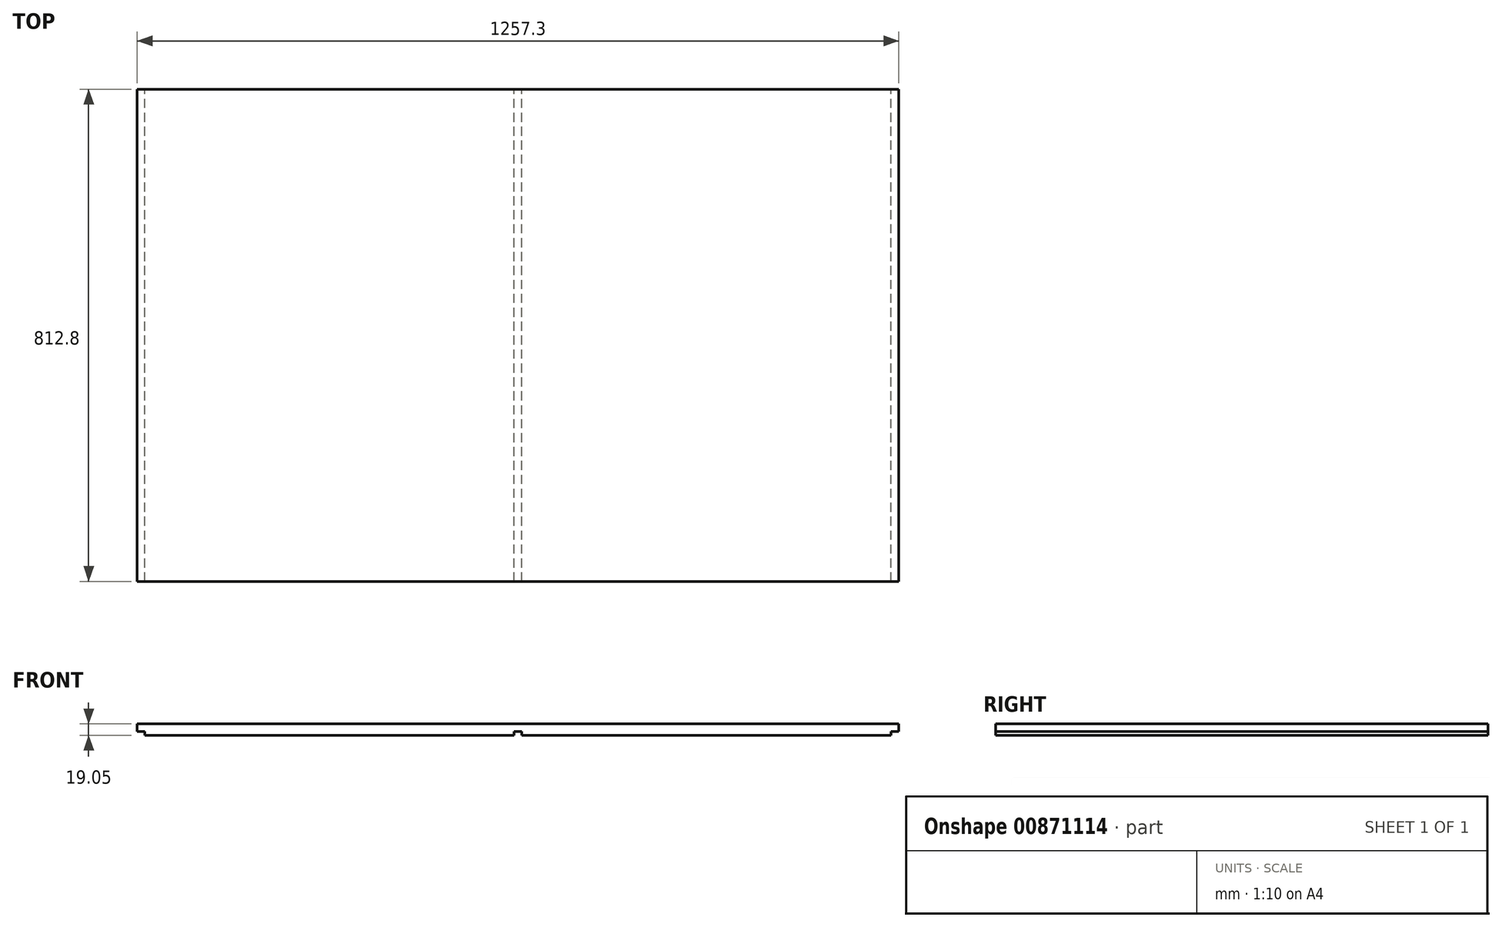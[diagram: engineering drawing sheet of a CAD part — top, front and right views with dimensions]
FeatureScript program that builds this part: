
annotation { "Feature Type Name" : "Feature", "Feature Type Description" : "" }
export const myFeature = defineFeature(function(context is Context, id is Id, definition is map)
    precondition{}
    {
        {
            var Q0;
            Q0=qCreatedBy(makeId("Front.planeOp"),FACE);
            var sketch = newSketch(context, id + "F0", { "sketchPlane" : qUnion([Q0])});
            skLineSegment(sketch, "E0.bottom", {"start": v(12.7, 0) * mm, "end": v(622.3, 0) * mm});
            skLineSegment(sketch, "E0.top", {"start": v(0, 19.05) * mm, "end": v(1257.3, 19.05) * mm});
            skLineSegment(sketch, "E0.left", {"start": v(0, 6.35) * mm, "end": v(0, 19.05) * mm});
            skLineSegment(sketch, "E0.right", {"start": v(1257.3, 6.35) * mm, "end": v(1257.3, 19.05) * mm});
            skLineSegment(sketch, "E1.top", {"start": v(0, 6.35) * mm, "end": v(12.7, 6.35) * mm});
            skLineSegment(sketch, "E1.right", {"start": v(12.7, 0) * mm, "end": v(12.7, 6.35) * mm});
            skLineSegment(sketch, "E2.top", {"start": v(622.3, 6.35) * mm, "end": v(635, 6.35) * mm});
            skLineSegment(sketch, "E2.left", {"start": v(622.3, 0) * mm, "end": v(622.3, 6.35) * mm});
            skLineSegment(sketch, "E2.right", {"start": v(635, 0) * mm, "end": v(635, 6.35) * mm});
            skLineSegment(sketch, "E3.trimOffspring", {"start": v(635, 0) * mm, "end": v(1244.6, 0) * mm});
            skLineSegment(sketch, "E4.top", {"start": v(1257.3, 6.35) * mm, "end": v(1244.6, 6.35) * mm});
            skLineSegment(sketch, "E4.right", {"start": v(1244.6, 0) * mm, "end": v(1244.6, 6.35) * mm});
            skSolve(sketch);
        }
        {
            var Q0;
            Q0 = qSketchRegion(id + "F0", true);
            extrude(context, id + "F1", {"entities" : qUnion([Q0]), "depth" : 812.8 * mm, "offsetDistance" : 25.4 * mm});
        }
    });
